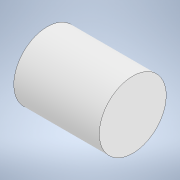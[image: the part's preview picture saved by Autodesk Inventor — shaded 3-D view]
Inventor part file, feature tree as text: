
AUTODESK INVENTOR PART (.ipt)
format: ipt  version: 2020.2 (Build 242310000, 310)  size: 98,816 bytes
history: native  units: mm
features: extrude x1, sketch x1
ambient origin geometry x8: Origin, YZ Plane, XZ Plane, XY Plane, X Axis, Y Axis, Z Axis, Center Point
bodies: Solid1 (feature_tree)
feature tree (2):
  extrude  "Extrusion1"  Depth=11.5mm TaperAngle=0.0deg
  sketch  "Sketch1"  dims[d0=9.0mm d1=11.5mm d2=0.0mm]
